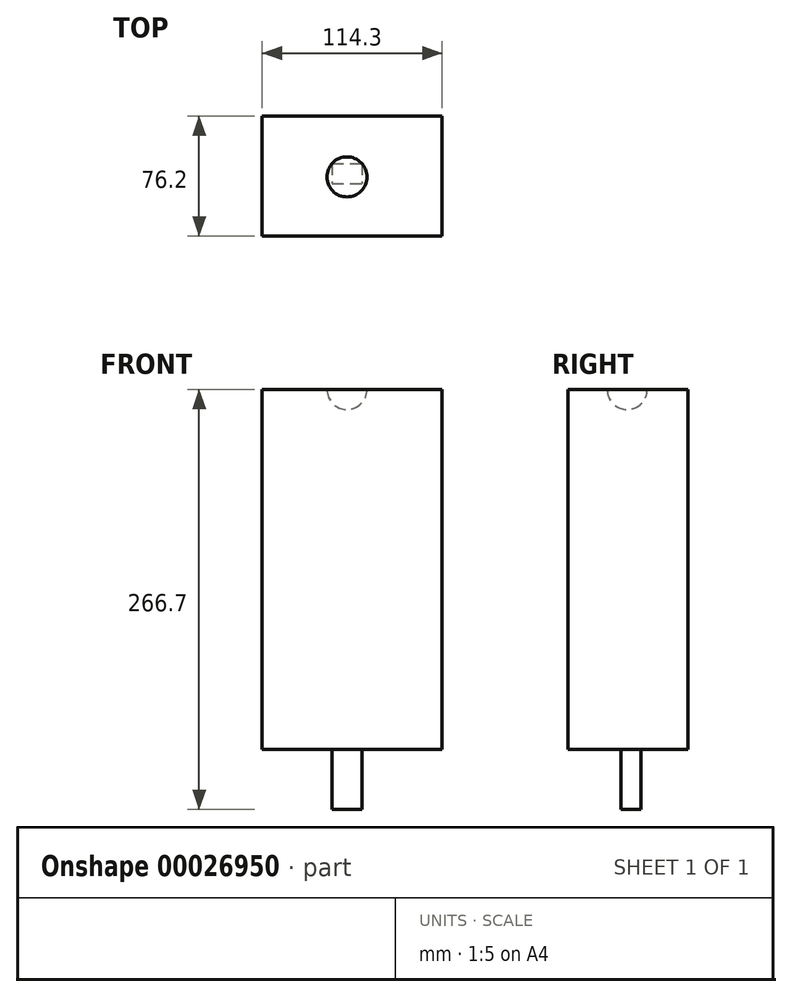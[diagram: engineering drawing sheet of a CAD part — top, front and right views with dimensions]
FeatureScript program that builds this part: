
annotation { "Feature Type Name" : "Feature", "Feature Type Description" : "" }
export const myFeature = defineFeature(function(context is Context, id is Id, definition is map)
    precondition{}
    {
        {
            var Q0;
            Q0=qCreatedBy(makeId("Top.planeOp"),FACE);
            var sketch = newSketch(context, id + "F0", { "sketchPlane" : qUnion([Q0])});
            skLineSegment(sketch, "E0.bottom", {"start": v(-9.53, 6.98) * mm, "end": v(9.52, 6.98) * mm});
            skLineSegment(sketch, "E0.top", {"start": v(-9.53, -5.72) * mm, "end": v(9.52, -5.71) * mm});
            skLineSegment(sketch, "E0.left", {"start": v(-9.53, 6.98) * mm, "end": v(-9.53, -5.72) * mm});
            skLineSegment(sketch, "E0.right", {"start": v(9.52, 6.98) * mm, "end": v(9.52, -5.72) * mm});
            skSolve(sketch);
        }
        {
            var Q0;
            Q0=makeQuery(id+"F0.imprint","IMPRINT",FACE,{"disambiguationData":[TD([[makeQuery(id+"F0.imprint","IMPRINT",EDGE,{"derivedFrom":sQuery(id+"F0.wireOp",EDGE,"E0.bottom")}),-1.0]])]});
            extrude(context, id + "F1", {"entities" : qUnion([Q0]), "depth" : 38.1 * mm});
        }
        {
            var Q0;
            Q0=qCreatedBy(makeId("Top.planeOp"),FACE);
            cPlane(context, id + "F2", {"entities" : qUnion([Q0]), "cplaneType" : CPlaneType.OFFSET, "offset" : 38.1 * mm, "width" : 152.4 * mm, "height" : 152.4 * mm});
        }
        {
            var Q0;
            Q0=qCreatedBy(id+"F2.planeOp",FACE);
            var sketch = newSketch(context, id + "F3", { "sketchPlane" : qUnion([Q0])});
            skLineSegment(sketch, "E1.bottom", {"start": v(-53.85, 37.06) * mm, "end": v(60.45, 37.06) * mm});
            skLineSegment(sketch, "E1.top", {"start": v(-53.85, -39.14) * mm, "end": v(60.45, -39.14) * mm});
            skLineSegment(sketch, "E1.left", {"start": v(-53.85, 37.06) * mm, "end": v(-53.85, -39.14) * mm});
            skLineSegment(sketch, "E1.right", {"start": v(60.45, 37.06) * mm, "end": v(60.45, -39.14) * mm});
            skSolve(sketch);
        }
        {
            var Q0;
            Q0=makeQuery(id+"F3.imprint","IMPRINT",FACE,{"disambiguationData":[TD([[makeQuery(id+"F3.imprint","IMPRINT",EDGE,{"derivedFrom":sQuery(id+"F3.wireOp",EDGE,"E1.bottom")}),-1.0]])]});
            extrude(context, id + "F4", {"entities" : qUnion([Q0]), "operationType" : NewBodyOperationType.ADD, "depth" : 228.6 * mm});
        }
        {
            var Q0;
            Q0=qCreatedBy(makeId("Front.planeOp"),FACE);
            cPlane(context, id + "F5", {"entities" : qUnion([Q0]), "cplaneType" : CPlaneType.OFFSET, "offset" : 38.1 * mm, "width" : 152.4 * mm, "height" : 152.4 * mm});
        }
        {
            var Q0;
            Q0=qCreatedBy(id+"F5.planeOp",FACE);
            var sketch = newSketch(context, id + "F6", { "sketchPlane" : qUnion([Q0])});
            skLineSegment(sketch, "E2", {"start": v(0, 317.18) * mm, "end": v(0, 279.08) * mm});
            skArc(sketch, "E3", {"start": v(0, 279.08) * mm, "mid": v(19.05, 298.13) * mm, "end": v(0, 317.18) * mm});
            skSolve(sketch);
        }
        {
            var Q0;
            Q0=qSketchRegion(id+"F6",true);
            var Q1;
            Q1=sQuery(id+"F6.wireOp",EDGE,"E2");
            revolve(context, id + "F7", {"operationType" : NewBodyOperationType.REMOVE, "entities" : qUnion([Q0]), "axis" : qUnion([Q1]), "revolveType" : RevolveType.FULL, "oppositeDirection" : true});
        }
        {
            var Q0;
            Q0=qCreatedBy(makeId("Top.planeOp"),FACE);
            cPlane(context, id + "F8", {"entities" : qUnion([Q0]), "cplaneType" : CPlaneType.OFFSET, "offset" : 266.7 * mm, "width" : 152.4 * mm, "height" : 152.4 * mm});
        }
        {
            var Q0;
            Q0=qCreatedBy(id+"F8.planeOp",FACE);
            var sketch = newSketch(context, id + "F9", { "sketchPlane" : qUnion([Q0])});
            skLineSegment(sketch, "E4", {"start": v(0, 11.13) * mm, "end": v(0, -14.27) * mm});
            skArc(sketch, "E5", {"start": v(0, -14.27) * mm, "mid": v(12.7, -1.57) * mm, "end": v(0, 11.13) * mm});
            skSolve(sketch);
        }
        {
            var Q0;
            Q0 = qSketchRegion(id + "F9", true);
            var Q1;
            Q1=sQuery(id+"F9.wireOp",EDGE,"E4");
            revolve(context, id + "F10", {"operationType" : NewBodyOperationType.REMOVE, "entities" : qUnion([Q0]), "axis" : qUnion([Q1]), "revolveType" : RevolveType.FULL, "oppositeDirection" : true});
        }
    });
